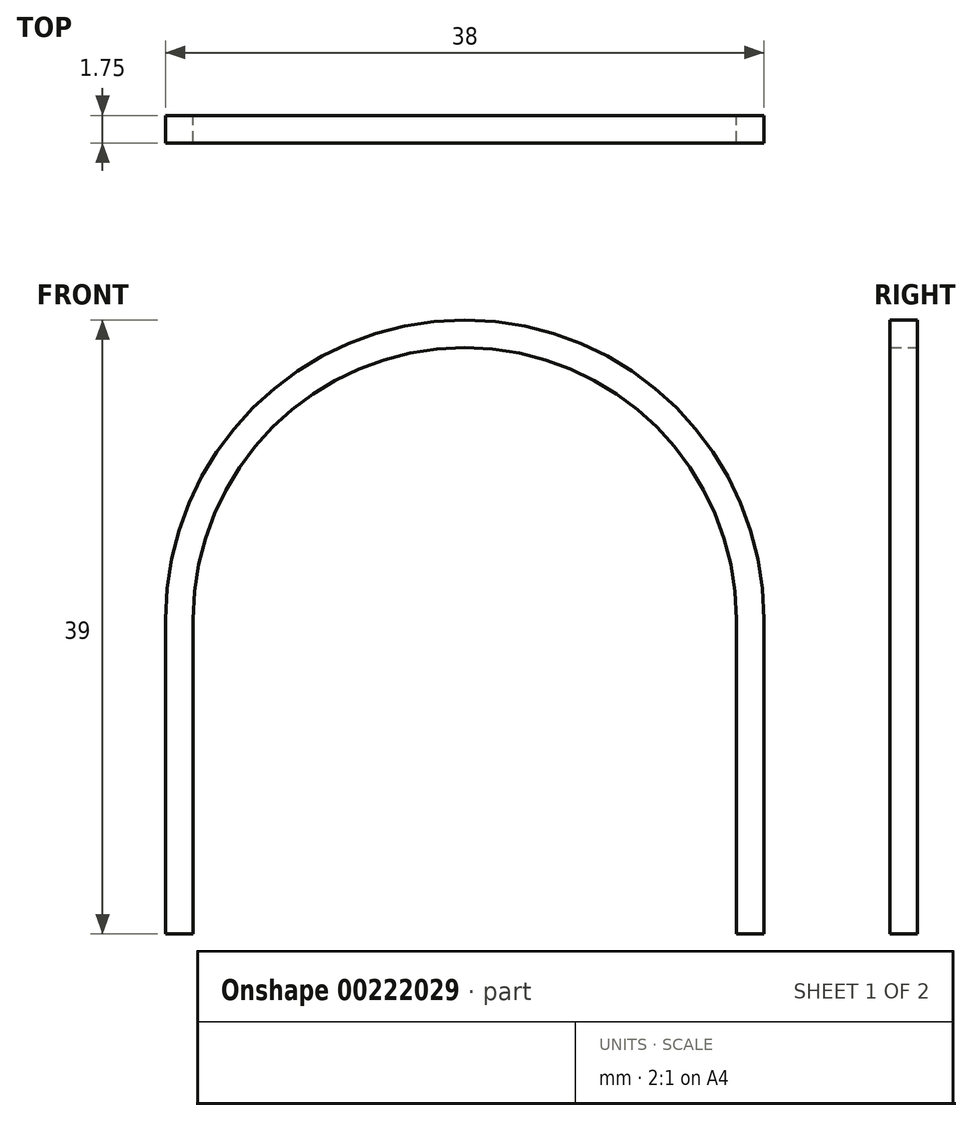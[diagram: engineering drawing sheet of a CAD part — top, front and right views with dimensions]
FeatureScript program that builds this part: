
annotation { "Feature Type Name" : "Feature", "Feature Type Description" : "" }
export const myFeature = defineFeature(function(context is Context, id is Id, definition is map)
    precondition{}
    {
        {
            var Q0;
            Q0=qCreatedBy(makeId("Front.planeOp"),FACE);
            var sketch = newSketch(context, id + "F0", { "sketchPlane" : qUnion([Q0])});
            skLineSegment(sketch, "E0", {"start": v(0, 0) * mm, "end": v(-19, 0) * mm, "construction": true});
            skLineSegment(sketch, "E1", {"start": v(-19, 0) * mm, "end": v(-19, 20) * mm, "construction": true});
            skLineSegment(sketch, "E2", {"start": v(0, 0) * mm, "end": v(19, 0) * mm, "construction": true});
            skLineSegment(sketch, "E3", {"start": v(19, 0) * mm, "end": v(19, 20) * mm, "construction": true});
            skLineSegment(sketch, "E4", {"start": v(-19, 0) * mm, "end": v(-19, 20) * mm});
            skLineSegment(sketch, "E5", {"start": v(19, 0) * mm, "end": v(19, 20) * mm});
            skArc(sketch, "E6", {"start": v(-19, 20) * mm, "mid": v(0, 39) * mm, "end": v(19, 20) * mm});
            skLineSegment(sketch, "E7.0", {"start": v(17.25, 0) * mm, "end": v(17.25, 20) * mm});
            skArc(sketch, "E7.1", {"start": v(-17.25, 20) * mm, "mid": v(0, 37.25) * mm, "end": v(17.25, 20) * mm});
            skLineSegment(sketch, "E7.2", {"start": v(-17.25, 0) * mm, "end": v(-17.25, 20) * mm});
            skLineSegment(sketch, "E8", {"start": v(-19, 0) * mm, "end": v(-17.25, 0) * mm});
            skLineSegment(sketch, "E9", {"start": v(17.25, 0) * mm, "end": v(19, 0) * mm});
            skSolve(sketch);
        }
        {
            var Q0;
            Q0 = qSketchRegion(id + "F0", true);
            extrude(context, id + "F1", {"entities" : qUnion([Q0]), "depth" : 1.75 * mm});
        }
    });
